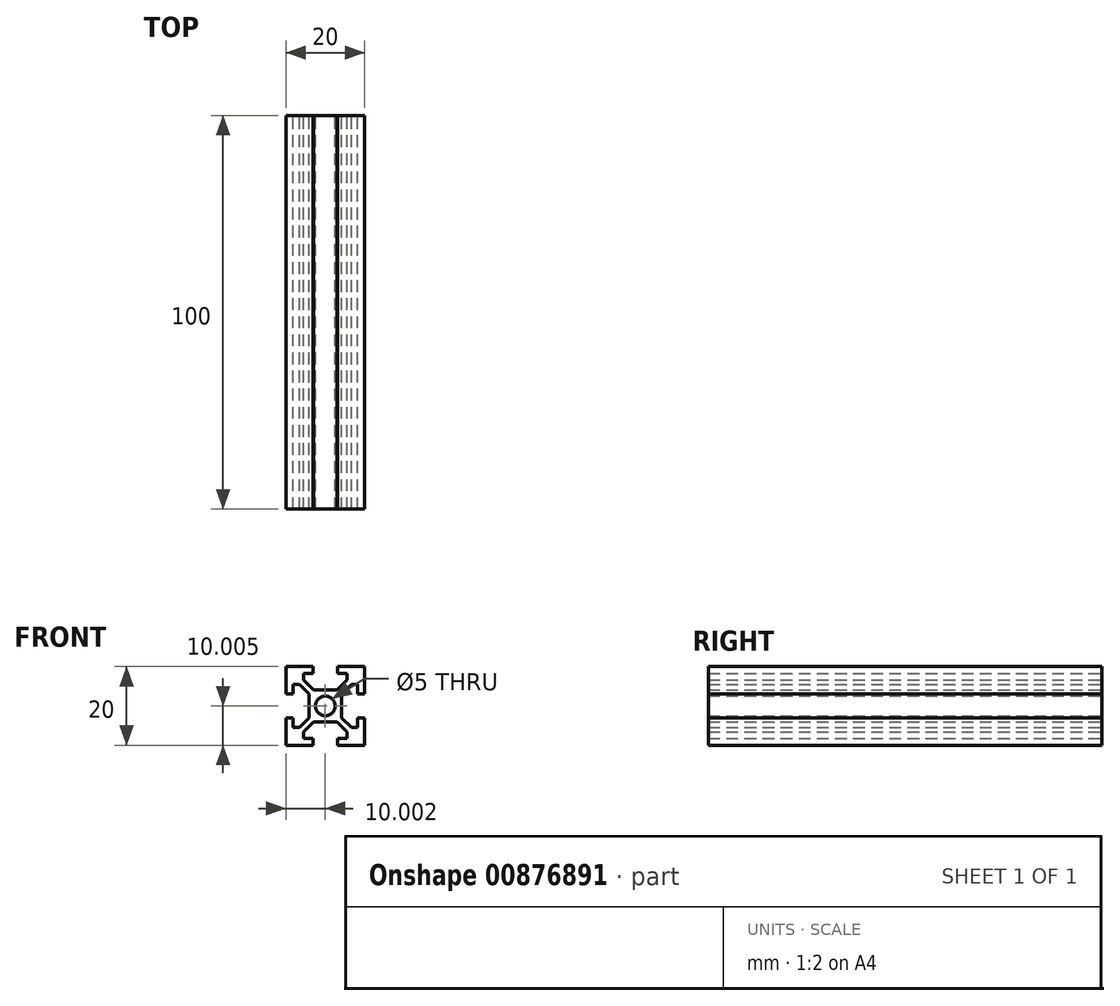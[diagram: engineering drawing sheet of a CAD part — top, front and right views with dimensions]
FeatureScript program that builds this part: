
annotation { "Feature Type Name" : "Feature", "Feature Type Description" : "" }
export const myFeature = defineFeature(function(context is Context, id is Id, definition is map)
    precondition{}
    {
        {
            var Q0;
            Q0=qCreatedBy(makeId("Front.planeOp"),FACE);
            var sketch = newSketch(context, id + "F0", { "sketchPlane" : qUnion([Q0])});
            skLineSegment(sketch, "E0.bottom", {"start": v(-28.18, 41.97) * mm, "end": v(-8.18, 41.97) * mm});
            skLineSegment(sketch, "E0.top", {"start": v(-28.18, 21.97) * mm, "end": v(-8.18, 21.97) * mm});
            skLineSegment(sketch, "E0.left", {"start": v(-28.18, 41.97) * mm, "end": v(-28.18, 21.97) * mm});
            skLineSegment(sketch, "E0.right", {"start": v(-8.18, 41.97) * mm, "end": v(-8.18, 21.97) * mm});
            skPoint(sketch, "E0.middle", {"position": v(-18.18, 31.97) * mm});
            skLineSegment(sketch, "E1", {"start": v(-9.98, 35.07) * mm, "end": v(-8.18, 35.07) * mm});
            skLineSegment(sketch, "E2.MirrorCS", {"start": v(-9.98, 28.87) * mm, "end": v(-8.18, 28.87) * mm});
            skLineSegment(sketch, "E3", {"start": v(-9.98, 35.07) * mm, "end": v(-9.98, 37.47) * mm});
            skLineSegment(sketch, "E4.MirrorCS", {"start": v(-9.98, 28.87) * mm, "end": v(-9.98, 26.47) * mm});
            skLineSegment(sketch, "E5", {"start": v(-9.98, 37.47) * mm, "end": v(-11.58, 37.47) * mm});
            skLineSegment(sketch, "E6.MirrorCS", {"start": v(-9.98, 26.47) * mm, "end": v(-11.58, 26.47) * mm});
            skCircle(sketch, "E7", {"center": v(-18.18, 31.97) * mm, "radius": 2.5 * mm});
            skLineSegment(sketch, "E8", {"start": v(-14.08, 34.97) * mm, "end": v(-14.08, 28.97) * mm});
            skLineSegment(sketch, "E9", {"start": v(-14.08, 34.97) * mm, "end": v(-11.58, 37.47) * mm});
            skLineSegment(sketch, "E10.MirrorCS", {"start": v(-14.08, 28.97) * mm, "end": v(-11.58, 26.47) * mm});
            skLineSegment(sketch, "E11.MirrorCS", {"start": v(-26.38, 35.07) * mm, "end": v(-28.18, 35.07) * mm});
            skLineSegment(sketch, "E12.MirrorCS", {"start": v(-26.38, 35.07) * mm, "end": v(-26.38, 37.47) * mm});
            skLineSegment(sketch, "E13.MirrorCS", {"start": v(-26.38, 37.47) * mm, "end": v(-24.78, 37.47) * mm});
            skLineSegment(sketch, "E14.MirrorCS", {"start": v(-22.28, 34.97) * mm, "end": v(-24.78, 37.47) * mm});
            skLineSegment(sketch, "E15.MirrorCS", {"start": v(-22.28, 34.97) * mm, "end": v(-22.28, 28.97) * mm});
            skLineSegment(sketch, "E16.MirrorCS", {"start": v(-22.28, 28.97) * mm, "end": v(-24.78, 26.47) * mm});
            skLineSegment(sketch, "E17.MirrorCS", {"start": v(-26.38, 26.47) * mm, "end": v(-24.78, 26.47) * mm});
            skLineSegment(sketch, "E18.MirrorCS", {"start": v(-26.38, 28.87) * mm, "end": v(-26.38, 26.47) * mm});
            skLineSegment(sketch, "E19.MirrorCS", {"start": v(-26.38, 28.87) * mm, "end": v(-28.18, 28.87) * mm});
            skLineSegment(sketch, "E20", {"start": v(-21.28, 41.97) * mm, "end": v(-21.28, 40.17) * mm});
            skLineSegment(sketch, "E21", {"start": v(-21.28, 40.17) * mm, "end": v(-23.68, 40.17) * mm});
            skLineSegment(sketch, "E22", {"start": v(-23.68, 40.17) * mm, "end": v(-23.68, 38.57) * mm});
            skLineSegment(sketch, "E23", {"start": v(-21.18, 36.07) * mm, "end": v(-18.18, 36.07) * mm});
            skLineSegment(sketch, "E24.MirrorCS", {"start": v(-15.08, 41.97) * mm, "end": v(-15.08, 40.17) * mm});
            skLineSegment(sketch, "E25.MirrorCS", {"start": v(-15.08, 40.17) * mm, "end": v(-12.68, 40.17) * mm});
            skLineSegment(sketch, "E26.MirrorCS", {"start": v(-12.68, 40.17) * mm, "end": v(-12.68, 38.57) * mm});
            skLineSegment(sketch, "E27.MirrorCS", {"start": v(-15.18, 36.07) * mm, "end": v(-18.18, 36.07) * mm});
            skLineSegment(sketch, "E28", {"start": v(-12.68, 38.57) * mm, "end": v(-15.18, 36.07) * mm});
            skLineSegment(sketch, "E29", {"start": v(-23.68, 38.57) * mm, "end": v(-21.18, 36.07) * mm});
            skLineSegment(sketch, "E30.MirrorCS", {"start": v(-21.28, 21.97) * mm, "end": v(-21.28, 23.77) * mm});
            skLineSegment(sketch, "E31.MirrorCS", {"start": v(-21.28, 23.77) * mm, "end": v(-23.68, 23.77) * mm});
            skLineSegment(sketch, "E32.MirrorCS", {"start": v(-23.68, 23.77) * mm, "end": v(-23.68, 25.37) * mm});
            skLineSegment(sketch, "E33.MirrorCS", {"start": v(-23.68, 25.37) * mm, "end": v(-21.18, 27.87) * mm});
            skLineSegment(sketch, "E34.MirrorCS", {"start": v(-15.08, 21.97) * mm, "end": v(-15.08, 23.77) * mm});
            skLineSegment(sketch, "E35.MirrorCS", {"start": v(-15.08, 23.77) * mm, "end": v(-12.68, 23.77) * mm});
            skLineSegment(sketch, "E36.MirrorCS", {"start": v(-12.68, 23.77) * mm, "end": v(-12.68, 25.37) * mm});
            skLineSegment(sketch, "E37.MirrorCS", {"start": v(-12.68, 25.37) * mm, "end": v(-15.18, 27.87) * mm});
            skLineSegment(sketch, "E38.MirrorCS", {"start": v(-15.18, 27.87) * mm, "end": v(-18.18, 27.87) * mm});
            skLineSegment(sketch, "E39.MirrorCS", {"start": v(-21.18, 27.87) * mm, "end": v(-18.18, 27.87) * mm});
            skSolve(sketch);
        }
        {
            var Q0;
            {var subQ5=sQuery(id+"F0.wireOp",EDGE,"E1");Q0=makeQuery(id+"F0.imprint","IMPRINT",FACE,{"disambiguationData":[TD([[makeQuery(id+"F0.imprint","IMPRINT",EDGE,{"derivedFrom":subQ5}),1.0]])]});}
            extrude(context, id + "F1", {"entities" : qUnion([Q0]), "depth" : 100 * mm, "offsetDistance" : 25 * mm});
        }
    });
